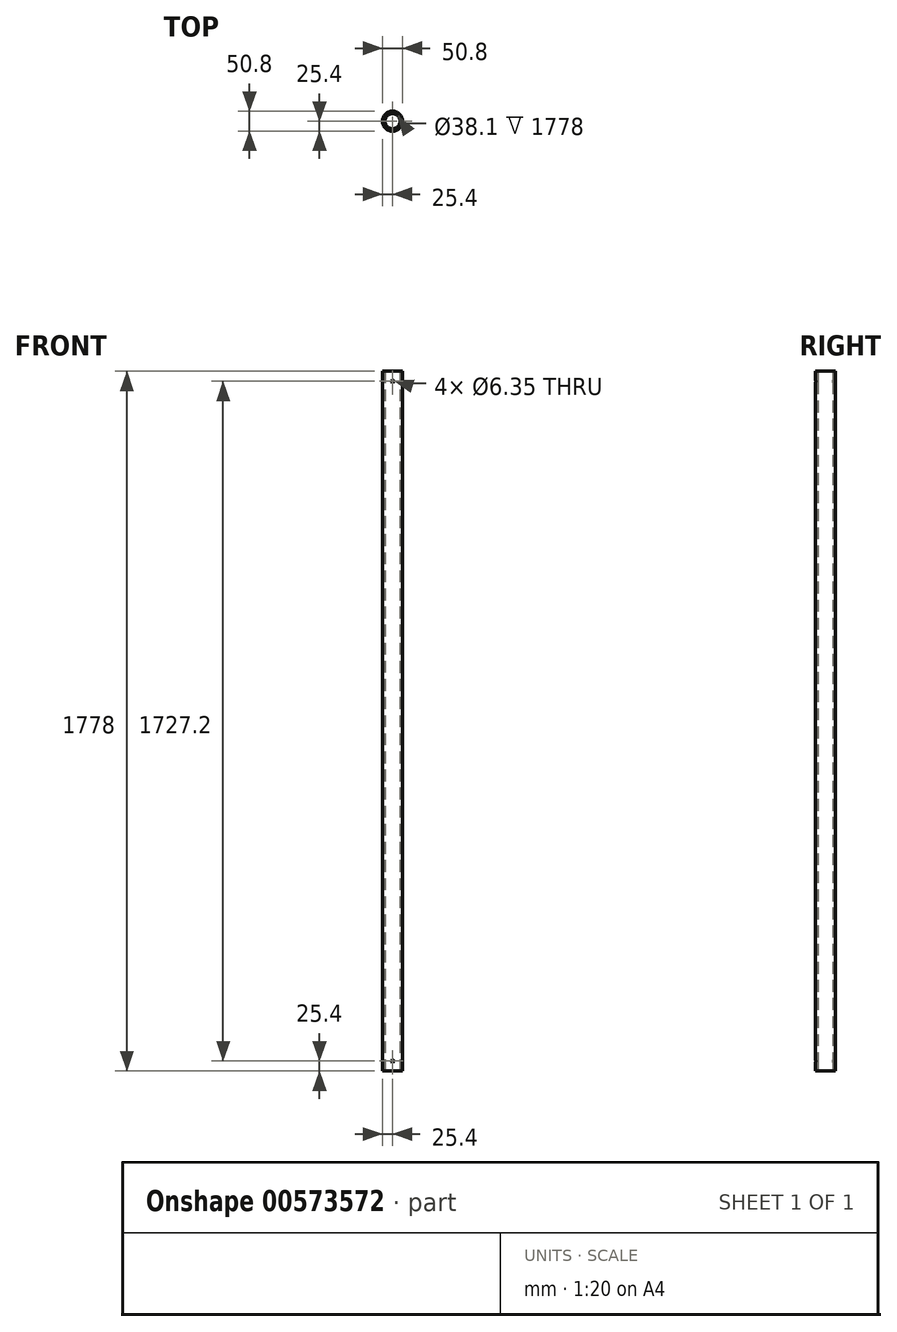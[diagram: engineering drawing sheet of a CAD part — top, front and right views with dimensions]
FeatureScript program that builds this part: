
annotation { "Feature Type Name" : "Feature", "Feature Type Description" : "" }
export const myFeature = defineFeature(function(context is Context, id is Id, definition is map)
    precondition{}
    {
        {
            var Q0;
            Q0=qCreatedBy(makeId("Top.planeOp"),FACE);
            var sketch = newSketch(context, id + "F0", { "sketchPlane" : qUnion([Q0])});
            skCircle(sketch, "E0", {"center": v(0, 0) * mm, "radius": 25.4 * mm});
            skCircle(sketch, "E1", {"center": v(0, 0) * mm, "radius": 19.05 * mm});
            skSolve(sketch);
        }
        {
            var Q0;
            Q0 = qSketchRegion(id + "F0", true);
            extrude(context, id + "F1", {"entities" : qUnion([Q0]), "depth" : 1778 * mm, "offsetDistance" : 25.4 * mm});
        }
        {
            var Q0;
            Q0=qCreatedBy(makeId("Front.planeOp"),FACE);
            var sketch = newSketch(context, id + "F2", { "sketchPlane" : qUnion([Q0])});
            skCircle(sketch, "E2", {"center": v(0, 25.4) * mm, "radius": 3.18 * mm});
            skCircle(sketch, "E3", {"center": v(0, 1752.6) * mm, "radius": 3.18 * mm});
            skSolve(sketch);
        }
        {
            var Q0;
            Q0 = qSketchRegion(id + "F2", true);
            extrude(context, id + "F3", {"entities" : qUnion([Q0]), "operationType" : NewBodyOperationType.REMOVE, "endBound" : BoundingType.THROUGH_ALL, "oppositeDirection" : true, "depth" : 25.4 * mm, "offsetDistance" : 25.4 * mm, "hasSecondDirection" : true, "secondDirectionBound" : SecondDirectionBoundingType.THROUGH_ALL, "secondDirectionOppositeDirection" : false, "secondDirectionDepth" : 25.4 * mm});
        }
    });
